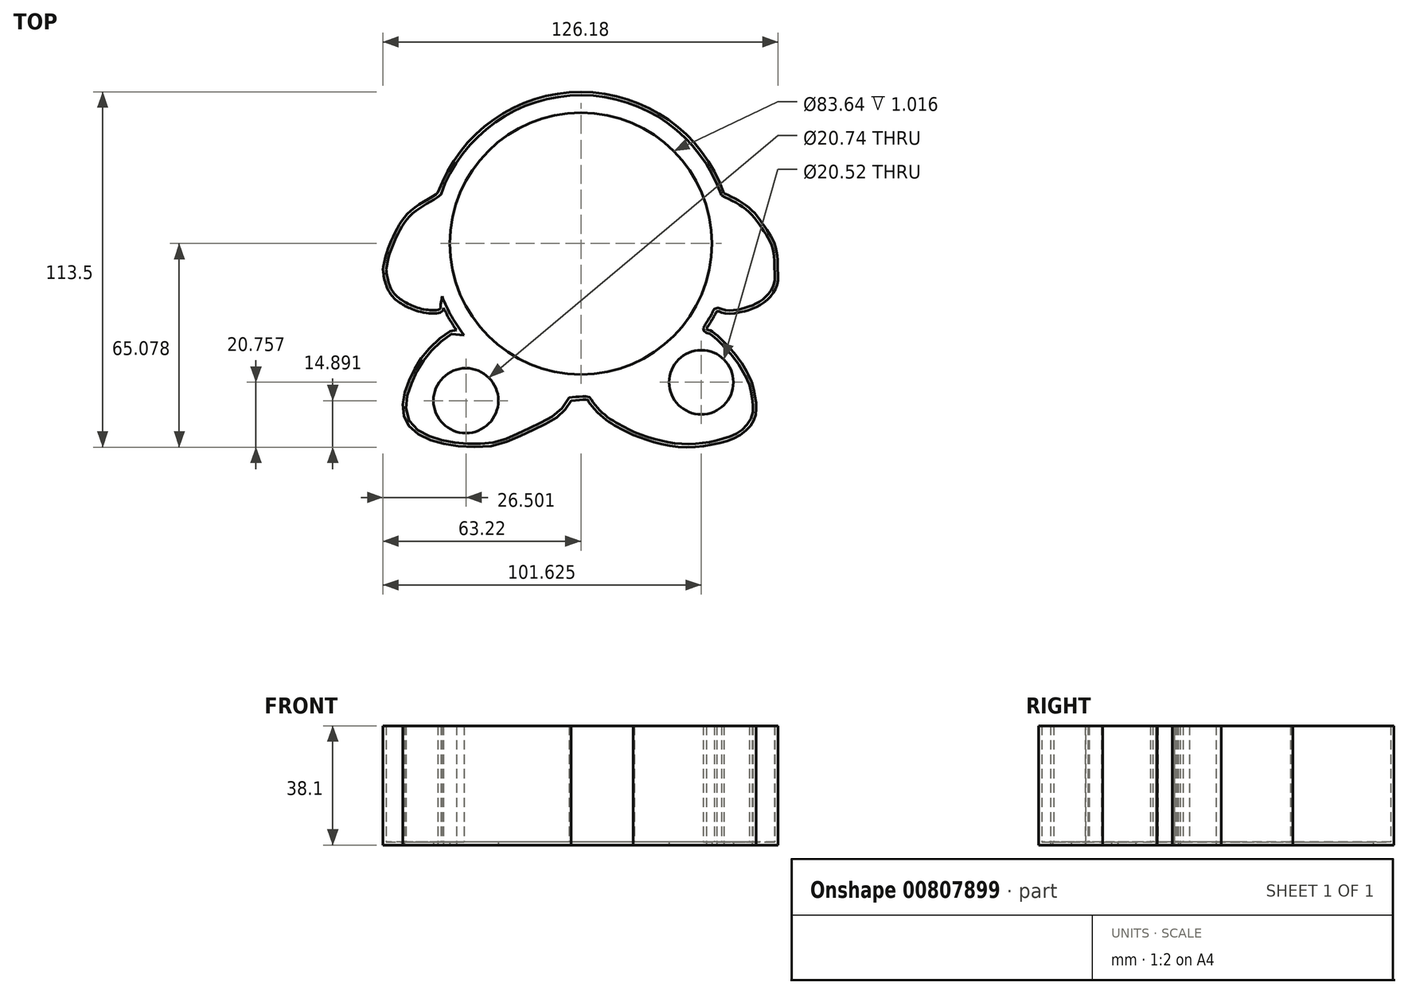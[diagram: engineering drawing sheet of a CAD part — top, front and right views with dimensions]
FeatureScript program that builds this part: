
annotation { "Feature Type Name" : "Feature", "Feature Type Description" : "" }
export const myFeature = defineFeature(function(context is Context, id is Id, definition is map)
    precondition{}
    {
        {
            var Q0;
            Q0=qCreatedBy(makeId("Top.planeOp"),FACE);
            var sketch = newSketch(context, id + "F0", { "sketchPlane" : qUnion([Q0])});
            skArc(sketch, "E0", {"start": v(-44.56, -12.67) * mm, "mid": v(-42.64, -16.36) * mm, "end": v(-40.41, -19.86) * mm});
            skPoint(sketch, "E0.first.point", {"position": v(0, 56.24) * mm});
            skPoint(sketch, "E0.second.point", {"position": v(0, -40.59) * mm});
            skPoint(sketch, "E0.third.point", {"position": v(6.9, -40) * mm});
            skFitSpline(sketch, "E1", {"points": [v(44.97, 23.93) * mm, v(50.42, 21.1) * mm, v(54.99, 17.27) * mm, v(58.44, 12.46) * mm, v(61.15, 7.65) * mm, v(62.14, 1.11) * mm], "startDerivative": vector(27.77, -12.98) * mm, "endDerivative": vector(2.22, -32.92) * mm});
            skFitSpline(sketch, "E2", {"points": [v(62.14, 1.11) * mm, v(62.14, -1.1) * mm, v(62.14, -4.56) * mm, v(59.43, -9.5) * mm, v(55.23, -12.46) * mm, v(50.42, -14.06) * mm, v(44.5, -14.31) * mm, v(42.6, -13.85) * mm, v(39.35, -19.4) * mm, v(40.3, -19.86) * mm, v(45.98, -24.67) * mm, v(50.91, -30.84) * mm, v(54, -36.76) * mm], "startDerivative": vector(-1.4, -36.74) * mm, "endDerivative": vector(28.17, -60.13) * mm});
            skFitSpline(sketch, "E3", {"points": [v(54, -36.76) * mm, v(55.19, -43.13) * mm, v(54.67, -48.16) * mm, v(50.77, -52.92) * mm, v(43.66, -55.87) * mm, v(33.52, -57.25) * mm, v(23.56, -55.87) * mm, v(15.93, -53.35) * mm], "startDerivative": vector(11.22, -49.43) * mm, "endDerivative": vector(-49.8, 18.28) * mm});
            skFitSpline(sketch, "E4", {"points": [v(15.93, -53.35) * mm, v(10.53, -50.53) * mm, v(5.56, -47.01) * mm, v(1.74, -42.57) * mm, v(1.53, -42.15) * mm, v(-3.85, -42.36) * mm], "startDerivative": vector(-23.3, 11.74) * mm, "endDerivative": vector(-32.77, -3.1) * mm});
            skFitSpline(sketch, "E5", {"points": [v(-3.85, -42.36) * mm, v(-6.74, -46.4) * mm, v(-12.22, -49.9) * mm, v(-19.35, -53.35) * mm, v(-28.66, -56.73) * mm, v(-40.03, -56.83) * mm, v(-48, -55.18) * mm, v(-54.61, -51.56) * mm, v(-57.2, -47.12) * mm, v(-57.3, -41.33) * mm, v(-55.13, -35.02) * mm, v(-52.03, -29.33) * mm, v(-47.17, -23.75) * mm, v(-41.8, -19.86) * mm, v(-40.41, -19.86) * mm], "startDerivative": vector(-39.85, -68.61) * mm, "endDerivative": vector(36.35, -8.52) * mm});
            skFitSpline(sketch, "E6", {"points": [v(-44.56, -12.67) * mm, v(-45.28, -14.06) * mm, v(-51.93, -13.98) * mm, v(-56.29, -12.36) * mm, v(-57.3, -11.84) * mm], "startDerivative": vector(-1.43, -8.98) * mm, "endDerivative": vector(-5.79, 2.92) * mm});
            skFitSpline(sketch, "E7", {"points": [v(-57.02, -12) * mm, v(-60.53, -9.42) * mm, v(-62.78, -5.72) * mm, v(-63.9, -0.55) * mm], "startDerivative": vector(-11.68, 7.2) * mm, "endDerivative": vector(-2.37, 15.13) * mm});
            skFitSpline(sketch, "E8", {"points": [v(-63.9, -0.55) * mm, v(-62.78, 4.69) * mm, v(-59.57, 12.18) * mm, v(-54.05, 19.07) * mm, v(-46.3, 24.08) * mm, v(-46, 24.88) * mm], "startDerivative": vector(4.27, 26.18) * mm, "endDerivative": vector(0.6, 9.36) * mm});
            skArc(sketch, "E9.trimOffspring", {"start": v(39.35, -19.4) * mm, "mid": v(41.07, -16.68) * mm, "end": v(42.6, -13.85) * mm});
            skArc(sketch, "E10.trimOffspring", {"start": v(44.97, 23.93) * mm, "mid": v(-0.62, 56.25) * mm, "end": v(-46.3, 24.08) * mm});
            skSolve(sketch);
        }
        {
            var Q0;
            Q0 = qSketchRegion(id + "F0", true);
            extrude(context, id + "F1", {"entities" : qUnion([Q0]), "depth" : 38.1 * mm, "offsetDistance" : 25.4 * mm});
        }
        {
            var Q0;
            Q0=makeQuery(id+"F1.opExtrude","CAP_FACE",FACE,{"disambiguationData":[OSD([sQuery(id+"F0.wireOp",EDGE,"E0"),sQuery(id+"F0.wireOp",EDGE,"E1"),sQuery(id+"F0.wireOp",EDGE,"E2"),sQuery(id+"F0.wireOp",EDGE,"E3"),sQuery(id+"F0.wireOp",EDGE,"E4"),sQuery(id+"F0.wireOp",EDGE,"E5"),sQuery(id+"F0.wireOp",EDGE,"E6"),sQuery(id+"F0.wireOp",EDGE,"E7"),sQuery(id+"F0.wireOp",EDGE,"E8"),sQuery(id+"F0.wireOp",EDGE,"E9.trimOffspring"),sQuery(id+"F0.wireOp",EDGE,"E10.trimOffspring")])],"isStart":false});
            shell(context, id + "F2", {"entities" : qUnion([Q0]), "thickness" : 1.02 * mm});
        }
        {
            var Q0;
            Q0=makeQuery(id+"F1.opExtrude","CAP_FACE",FACE,{"disambiguationData":[OSD([sQuery(id+"F0.wireOp",EDGE,"E0"),sQuery(id+"F0.wireOp",EDGE,"E1"),sQuery(id+"F0.wireOp",EDGE,"E2"),sQuery(id+"F0.wireOp",EDGE,"E3"),sQuery(id+"F0.wireOp",EDGE,"E4"),sQuery(id+"F0.wireOp",EDGE,"E5"),sQuery(id+"F0.wireOp",EDGE,"E6"),sQuery(id+"F0.wireOp",EDGE,"E7"),sQuery(id+"F0.wireOp",EDGE,"E8"),sQuery(id+"F0.wireOp",EDGE,"E9.trimOffspring"),sQuery(id+"F0.wireOp",EDGE,"E10.trimOffspring")])],"isStart":true});
            var sketch = newSketch(context, id + "F3", { "sketchPlane" : qUnion([Q0])});
            skCircle(sketch, "E11", {"center": v(-0.7, -7.83) * mm, "radius": 41.82 * mm});
            skCircle(sketch, "E12", {"center": v(-37.4, 42.36) * mm, "radius": 10.37 * mm});
            skCircle(sketch, "E13", {"center": v(37.71, 36.5) * mm, "radius": 10.26 * mm});
            skSolve(sketch);
        }
        {
            var Q0;
            Q0 = qSketchRegion(id + "F3", true);
            extrude(context, id + "F4", {"entities" : qUnion([Q0]), "operationType" : NewBodyOperationType.REMOVE, "oppositeDirection" : true, "depth" : 25.4 * mm, "offsetDistance" : 25.4 * mm});
        }
    });
